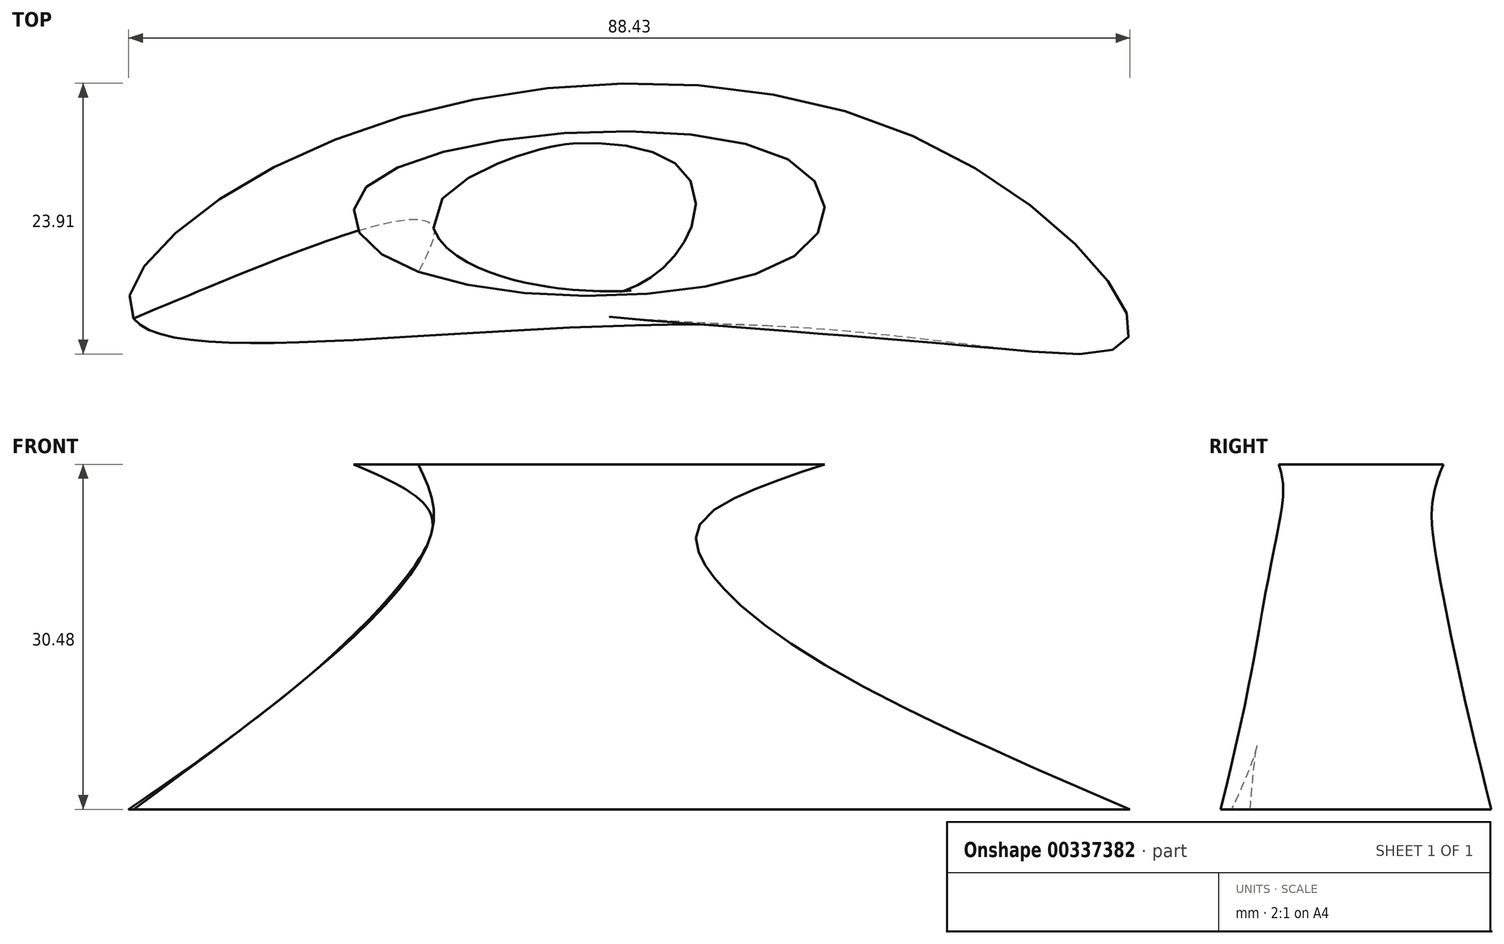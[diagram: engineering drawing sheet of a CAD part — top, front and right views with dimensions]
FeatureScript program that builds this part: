
annotation { "Feature Type Name" : "Feature", "Feature Type Description" : "" }
export const myFeature = defineFeature(function(context is Context, id is Id, definition is map)
    precondition{}
    {
        {
            var Q0;
            Q0=qCreatedBy(makeId("Top.planeOp"),FACE);
            var sketch = newSketch(context, id + "F0", { "sketchPlane" : qUnion([Q0])});
            skFitSpline(sketch, "E0", {"points": [v(-41.45, 19.63) * mm, v(-28.3, 33.38) * mm, v(26.9, 35.97) * mm, v(46.43, 18.03) * mm, v(13.15, 19.03) * mm, v(-41.45, 19.63) * mm]});
            skSolve(sketch);
        }
        {
            var Q0;
            Q0=qCreatedBy(makeId("Top.planeOp"),FACE);
            cPlane(context, id + "F1", {"entities" : qUnion([Q0]), "cplaneType" : CPlaneType.OFFSET, "offset" : 25.4 * mm, "width" : 152.4 * mm, "height" : 152.4 * mm});
        }
        {
            var Q0;
            Q0=qCreatedBy(id+"F1.planeOp",FACE);
            var sketch = newSketch(context, id + "F2", { "sketchPlane" : qUnion([Q0])});
            skFitSpline(sketch, "E1", {"points": [v(-14.95, 27.6) * mm, v(-4.98, 34.77) * mm, v(8.37, 31.19) * mm, v(2.6, 22.22) * mm, v(-14.95, 27.6) * mm]});
            skSolve(sketch);
        }
        {
            var Q0;
            Q0=qCreatedBy(id+"F1.planeOp",FACE);
            cPlane(context, id + "F3", {"entities" : qUnion([Q0]), "cplaneType" : CPlaneType.OFFSET, "offset" : 5.08 * mm, "width" : 152.4 * mm, "height" : 152.4 * mm});
        }
        {
            var Q0;
            Q0=qCreatedBy(id+"F3.planeOp",FACE);
            var sketch = newSketch(context, id + "F4", { "sketchPlane" : qUnion([Q0])});
            skFitSpline(sketch, "E2", {"points": [v(-20.72, 31.39) * mm, v(16.54, 33.58) * mm, v(17.54, 25.6) * mm, v(-18.33, 24.61) * mm, v(-20.72, 31.39) * mm]});
            skSolve(sketch);
        }
        {
            var Q0;
            Q0 = qSketchRegion(id + "F0", true);
            var Q1;
            Q1 = qSketchRegion(id + "F2", true);
            var Q2;
            Q2 = qSketchRegion(id + "F4", true);
            loft(context, id + "F5", {"sheetProfilesArray" : [{ "sheetProfileEntities" : qUnion([Q0]) }, { "sheetProfileEntities" : qUnion([Q1]) }, { "sheetProfileEntities" : qUnion([Q2]) }]});
        }
    });
